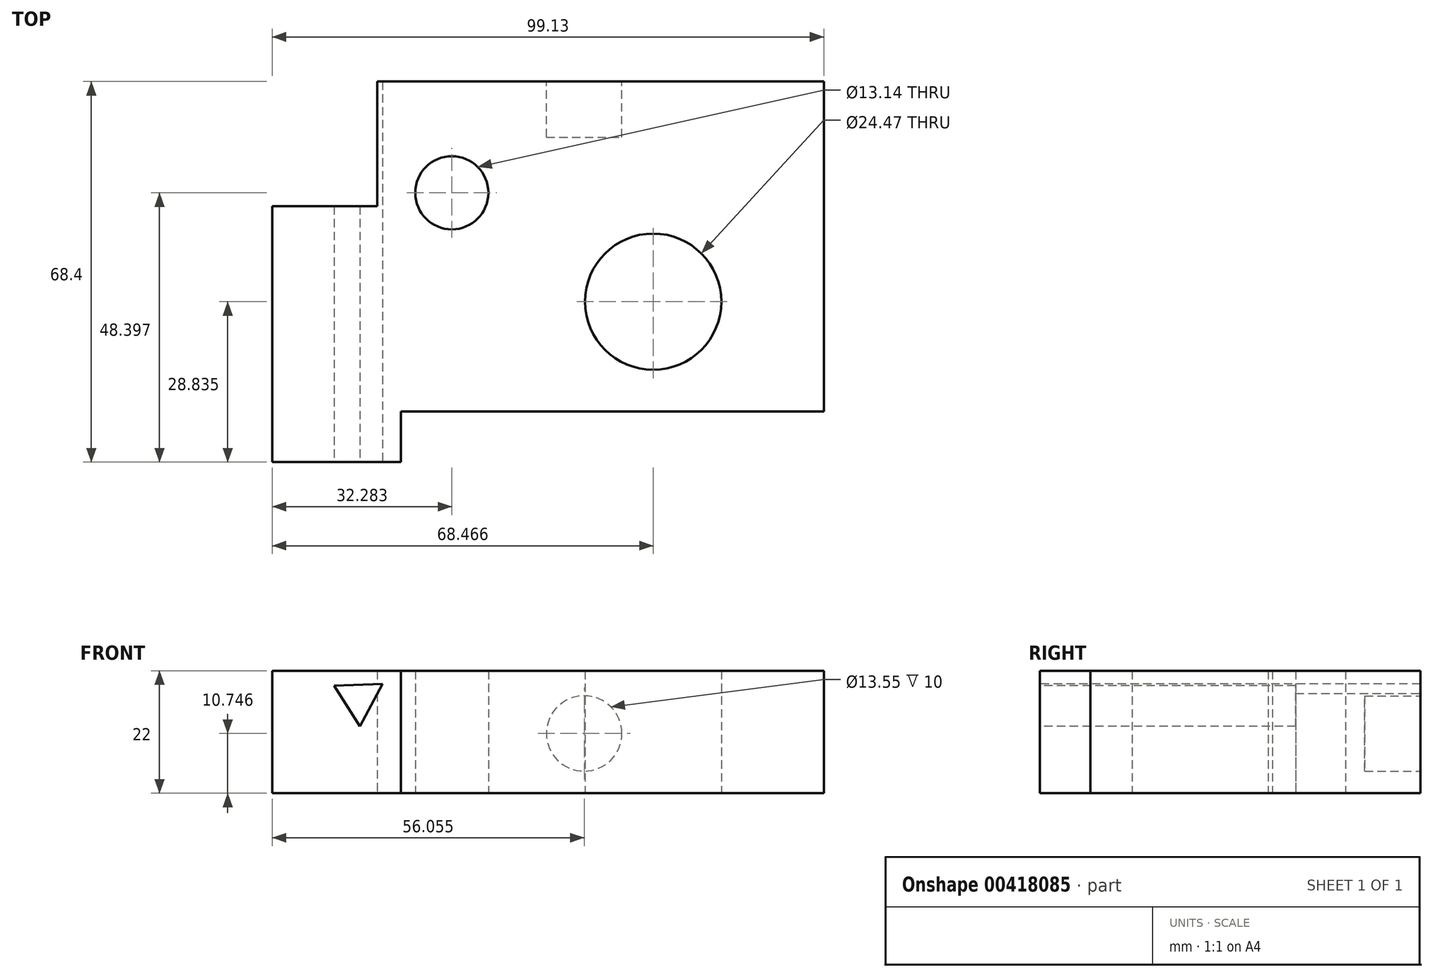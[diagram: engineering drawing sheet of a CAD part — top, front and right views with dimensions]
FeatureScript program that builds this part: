
annotation { "Feature Type Name" : "Feature", "Feature Type Description" : "" }
export const myFeature = defineFeature(function(context is Context, id is Id, definition is map)
    precondition{}
    {
        {
            var Q0;
            Q0=qCreatedBy(makeId("Top.planeOp"),FACE);
            var sketch = newSketch(context, id + "F0", { "sketchPlane" : qUnion([Q0])});
            skLineSegment(sketch, "E0.bottom", {"start": v(13.88, -32.76) * mm, "end": v(-66.35, -32.76) * mm});
            skLineSegment(sketch, "E0.top", {"start": v(13.88, 26.55) * mm, "end": v(-66.35, 26.55) * mm});
            skLineSegment(sketch, "E0.left", {"start": v(13.88, -32.76) * mm, "end": v(13.88, 26.55) * mm});
            skLineSegment(sketch, "E0.right", {"start": v(-66.35, -32.76) * mm, "end": v(-66.35, 26.55) * mm});
            skPoint(sketch, "E0.middle", {"position": v(-26.23, -3.1) * mm});
            skCircle(sketch, "E1", {"center": v(-52.97, 6.55) * mm, "radius": 6.57 * mm});
            skCircle(sketch, "E2", {"center": v(-16.78, -13.02) * mm, "radius": 12.24 * mm});
            skLineSegment(sketch, "E3.bottom", {"start": v(-62.15, -41.85) * mm, "end": v(-85.25, -41.85) * mm});
            skLineSegment(sketch, "E3.top", {"start": v(-66.35, 4.14) * mm, "end": v(-85.25, 4.14) * mm});
            skLineSegment(sketch, "E3.left", {"start": v(-62.15, -41.85) * mm, "end": v(-62.15, -32.76) * mm});
            skLineSegment(sketch, "E3.right", {"start": v(-85.25, -41.85) * mm, "end": v(-85.25, 4.14) * mm});
            skPoint(sketch, "E3.middle", {"position": v(-73.7, -18.86) * mm});
            skPoint(sketch, "E4.orphan", {"position": v(-62.15, 4.14) * mm});
            skSolve(sketch);
        }
        {
            var Q0;
            Q0 = qSketchRegion(id + "F0", true);
            extrude(context, id + "F1", {"entities" : qUnion([Q0]), "depth" : 22 * mm});
        }
        {
            var Q0;
            Q0=makeQuery(id+"F1.opExtrude","SWEPT_FACE",FACE,{"disambiguationData":[OSD([sQuery(id+"F0.wireOp",EDGE,"E3.bottom")])]});
            var sketch = newSketch(context, id + "F2", { "sketchPlane" : qUnion([Q0])});
            skCircle(sketch, "E5.cCircle", {"center": v(-69.68, 17) * mm, "radius": 2.5 * mm, "construction": true});
            skLineSegment(sketch, "E5.0", {"start": v(-65.45, 19.66) * mm, "end": v(-69.48, 12) * mm});
            skLineSegment(sketch, "E5.1", {"start": v(-69.48, 12) * mm, "end": v(-74.1, 19.32) * mm});
            skLineSegment(sketch, "E5.2", {"start": v(-74.1, 19.32) * mm, "end": v(-65.45, 19.66) * mm});
            skPoint(sketch, "E5.0.midPoint", {"position": v(-67.46, 15.83) * mm});
            skSolve(sketch);
        }
        {
            var Q0;
            Q0 = qSketchRegion(id + "F2", true);
            extrude(context, id + "F3", {"entities" : qUnion([Q0]), "operationType" : NewBodyOperationType.REMOVE, "endBound" : BoundingType.THROUGH_ALL, "oppositeDirection" : true, "depth" : 54.3 * mm});
        }
        {
            var Q0;
            Q0=makeQuery(id+"F1.opExtrude","SWEPT_FACE",FACE,{"disambiguationData":[OSD([sQuery(id+"F0.wireOp",EDGE,"E0.top")])]});
            var sketch = newSketch(context, id + "F4", { "sketchPlane" : qUnion([Q0])});
            skCircle(sketch, "E6", {"center": v(29.2, 10.75) * mm, "radius": 6.77 * mm});
            skSolve(sketch);
        }
        {
            var Q0;
            Q0 = qSketchRegion(id + "F4", true);
            extrude(context, id + "F5", {"entities" : qUnion([Q0]), "operationType" : NewBodyOperationType.REMOVE, "oppositeDirection" : true, "depth" : 10 * mm});
        }
    });
